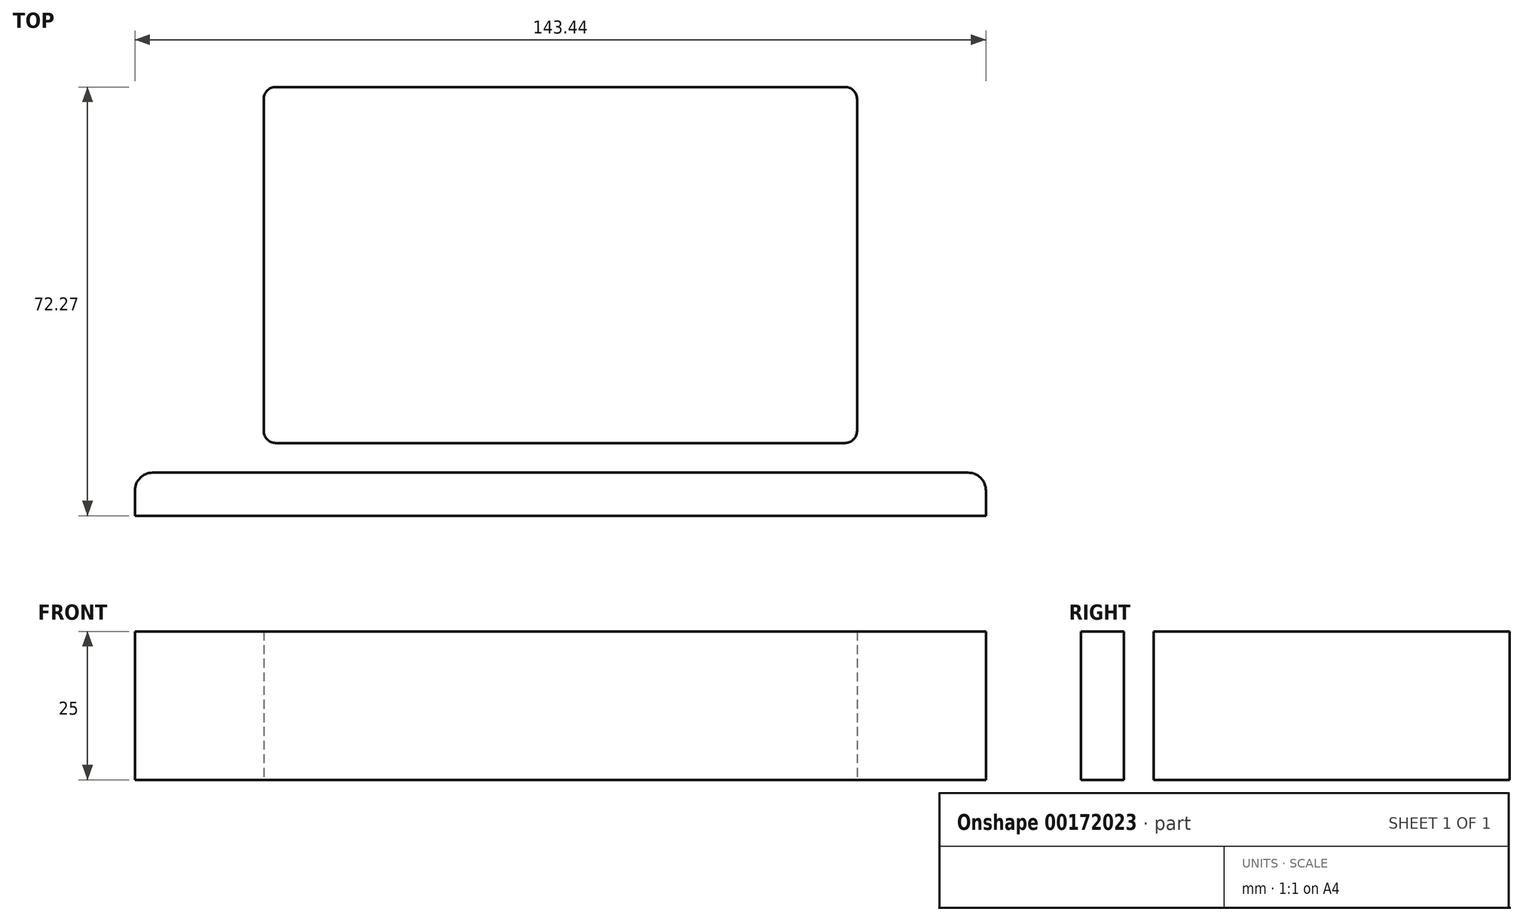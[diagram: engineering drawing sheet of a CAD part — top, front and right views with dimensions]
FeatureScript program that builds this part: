
annotation { "Feature Type Name" : "Feature", "Feature Type Description" : "" }
export const myFeature = defineFeature(function(context is Context, id is Id, definition is map)
    precondition{}
    {
        {
            var Q0;
            Q0=qCreatedBy(makeId("Top.planeOp"),FACE);
            var sketch = newSketch(context, id + "F0", { "sketchPlane" : qUnion([Q0])});
            skLineSegment(sketch, "E0.bottom", {"start": v(-48, 30) * mm, "end": v(48, 30) * mm});
            skLineSegment(sketch, "E0.top", {"start": v(-48, -30) * mm, "end": v(48, -30) * mm});
            skLineSegment(sketch, "E0.left", {"start": v(-50, 28) * mm, "end": v(-50, -28) * mm});
            skLineSegment(sketch, "E0.right", {"start": v(50, 28) * mm, "end": v(50, -28) * mm});
            skLineSegment(sketch, "E1.0", {"start": v(-50, 35) * mm, "end": v(50, 35) * mm});
            skLineSegment(sketch, "E1.1", {"start": v(-55, 30) * mm, "end": v(-55, -35) * mm});
            skLineSegment(sketch, "E1.2", {"start": v(-55, -35) * mm, "end": v(55, -35) * mm});
            skLineSegment(sketch, "E1.3", {"start": v(55, 30) * mm, "end": v(55, -35) * mm});
            skLineSegment(sketch, "E2.bottom", {"start": v(-68.72, -35) * mm, "end": v(68.72, -35) * mm});
            skLineSegment(sketch, "E2.top", {"start": v(-71.72, -42.27) * mm, "end": v(71.72, -42.27) * mm});
            skLineSegment(sketch, "E2.left", {"start": v(-71.72, -38) * mm, "end": v(-71.72, -42.27) * mm});
            skLineSegment(sketch, "E2.right", {"start": v(71.72, -38) * mm, "end": v(71.72, -42.27) * mm});
            skLineSegment(sketch, "E3", {"start": v(-71.72, -42.27) * mm, "end": v(-67, -45.41) * mm});
            skLineSegment(sketch, "E4", {"start": v(-67, -45.41) * mm, "end": v(0, -45.41) * mm});
            skLineSegment(sketch, "E5.MirrorCS", {"start": v(67, -45.41) * mm, "end": v(0, -45.41) * mm});
            skLineSegment(sketch, "E6.MirrorCS", {"start": v(71.72, -42.27) * mm, "end": v(67, -45.41) * mm});
            skPoint(sketch, "E7.visualSharp", {"position": v(-55, 35) * mm});
            skArc(sketch, "E7.filletArc", {"start": v(-50, 35) * mm, "mid": v(-53.54, 33.54) * mm, "end": v(-55, 30) * mm});
            skPoint(sketch, "E8.visualSharp", {"position": v(55, 35) * mm});
            skArc(sketch, "E8.filletArc", {"start": v(55, 30) * mm, "mid": v(53.54, 33.54) * mm, "end": v(50, 35) * mm});
            skArc(sketch, "E9.filletArc", {"start": v(50, 28) * mm, "mid": v(49.41, 29.41) * mm, "end": v(48, 30) * mm});
            skArc(sketch, "E10.filletArc", {"start": v(-48, 30) * mm, "mid": v(-49.41, 29.41) * mm, "end": v(-50, 28) * mm});
            skPoint(sketch, "E11.visualSharp", {"position": v(-50, -30) * mm});
            skArc(sketch, "E11.filletArc", {"start": v(-50, -28) * mm, "mid": v(-49.41, -29.41) * mm, "end": v(-48, -30) * mm});
            skPoint(sketch, "E12.visualSharp", {"position": v(50, -30) * mm});
            skArc(sketch, "E12.filletArc", {"start": v(48, -30) * mm, "mid": v(49.41, -29.41) * mm, "end": v(50, -28) * mm});
            skPoint(sketch, "E13.visualSharp", {"position": v(-71.72, -35) * mm});
            skArc(sketch, "E13.filletArc", {"start": v(-68.72, -35) * mm, "mid": v(-70.84, -35.88) * mm, "end": v(-71.72, -38) * mm});
            skPoint(sketch, "E14.visualSharp", {"position": v(71.72, -35) * mm});
            skArc(sketch, "E14.filletArc", {"start": v(71.72, -38) * mm, "mid": v(70.84, -35.88) * mm, "end": v(68.72, -35) * mm});
            skSolve(sketch);
        }
        {
            var Q0;
            Q0=makeQuery(id+"F0.imprint","IMPRINT",FACE,{"disambiguationData":[TD([[makeQuery(id+"F0.imprint","IMPRINT",EDGE,{"derivedFrom":sQuery(id+"F0.wireOp",EDGE,"E0.bottom")}),-1.0]])]});
            var Q1;
            Q1=makeQuery(id+"F0.imprint","IMPRINT",FACE,{"disambiguationData":[TD([[makeQuery(id+"F0.imprint","IMPRINT",EDGE,{"derivedFrom":sQuery(id+"F0.wireOp",EDGE,"E2.top")}),1.0]])]});
            extrude(context, id + "F1", {"entities" : qUnion([Q0, Q1]), "depth" : 25 * mm});
        }
    });
